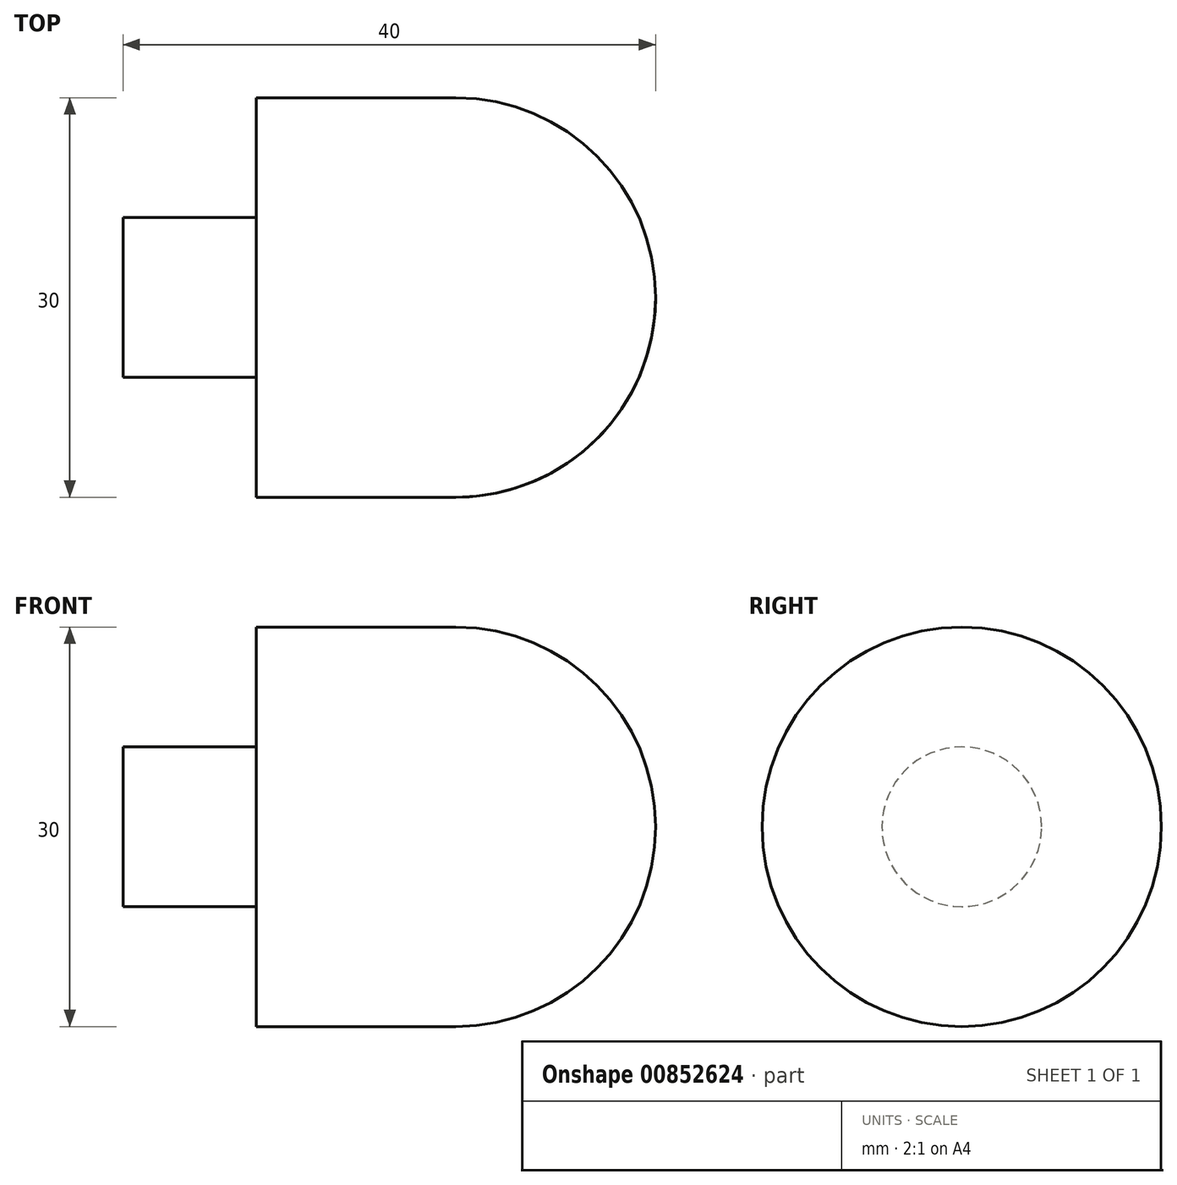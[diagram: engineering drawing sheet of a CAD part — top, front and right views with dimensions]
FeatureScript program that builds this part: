
annotation { "Feature Type Name" : "Feature", "Feature Type Description" : "" }
export const myFeature = defineFeature(function(context is Context, id is Id, definition is map)
    precondition{}
    {
        {
            var Q0;
            Q0=qCreatedBy(makeId("Top.planeOp"),FACE);
            var sketch = newSketch(context, id + "F0", { "sketchPlane" : qUnion([Q0])});
            skLineSegment(sketch, "E0", {"start": v(0, 0) * mm, "end": v(0, 6) * mm});
            skLineSegment(sketch, "E1", {"start": v(0, 6) * mm, "end": v(10, 6) * mm});
            skLineSegment(sketch, "E2", {"start": v(10, 6) * mm, "end": v(10, 15) * mm});
            skLineSegment(sketch, "E3", {"start": v(10, 15) * mm, "end": v(25, 15) * mm});
            skLineSegment(sketch, "E4", {"start": v(25, 15) * mm, "end": v(25, 15) * mm});
            skLineSegment(sketch, "E5", {"start": v(40, 0) * mm, "end": v(40, 0) * mm});
            skLineSegment(sketch, "E6", {"start": v(40, 0) * mm, "end": v(0, 0) * mm});
            skPoint(sketch, "E7.visualSharp", {"position": v(40, 15) * mm});
            skArc(sketch, "E7.filletArc", {"start": v(40, 0) * mm, "mid": v(35.6, 10.6) * mm, "end": v(25, 15) * mm});
            skSolve(sketch);
        }
        {
            var Q0;
            Q0 = qSketchRegion(id + "F0", true);
            var Q1;
            Q1=sQuery(id+"F0.wireOp",EDGE,"E6");
            revolve(context, id + "F1", {"surfaceOperationType" : NewSurfaceOperationType.NEW, "entities" : qUnion([Q0]), "axis" : qUnion([Q1]), "revolveType" : RevolveType.FULL});
        }
    });
